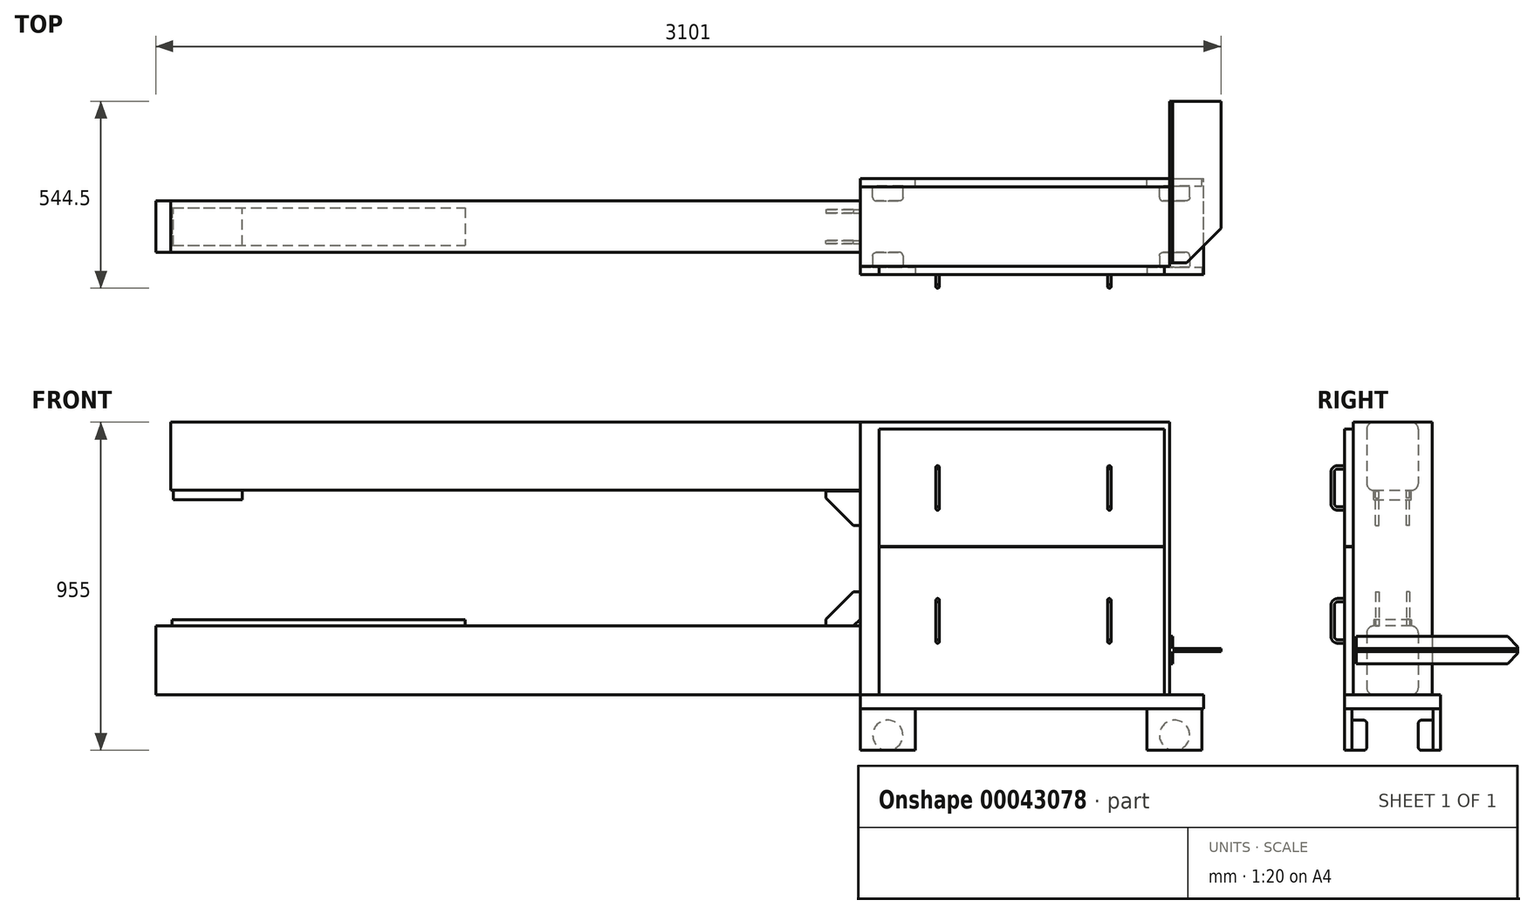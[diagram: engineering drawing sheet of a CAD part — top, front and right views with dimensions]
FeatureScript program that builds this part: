
annotation { "Feature Type Name" : "Feature", "Feature Type Description" : "" }
export const myFeature = defineFeature(function(context is Context, id is Id, definition is map)
    precondition{}
    {
        {
            var Q0;
            Q0=qCreatedBy(makeId("Front.planeOp"),FACE);
            var sketch = newSketch(context, id + "F0", { "sketchPlane" : qUnion([Q0])});
            skLineSegment(sketch, "E0.rect.bottom", {"start": v(-1025.5, 100) * mm, "end": v(1025.5, 100) * mm});
            skLineSegment(sketch, "E0.rect.top", {"start": v(-1025.5, -100) * mm, "end": v(1925.5, -100) * mm});
            skLineSegment(sketch, "E0.rect.left", {"start": v(-1025.5, 100) * mm, "end": v(-1025.5, -100) * mm});
            skLineSegment(sketch, "E0.rect.right", {"start": v(1025.5, 100) * mm, "end": v(1025.5, -100) * mm});
            skPoint(sketch, "E0.rect.middle", {"position": v(0, 0) * mm});
            skLineSegment(sketch, "E1.0", {"start": v(-982.5, 495) * mm, "end": v(1025.5, 495) * mm});
            skLineSegment(sketch, "E2.0", {"start": v(-982.5, 693) * mm, "end": v(1925.5, 693) * mm});
            skLineSegment(sketch, "E3.0", {"start": v(-982.5, 693) * mm, "end": v(-982.5, 495) * mm});
            skLineSegment(sketch, "E4", {"start": v(1025.5, 693) * mm, "end": v(1025.5, -100) * mm});
            skLineSegment(sketch, "E5.0", {"start": v(1925.5, 693) * mm, "end": v(1925.5, -100) * mm});
            skSolve(sketch);
        }
        {
            var Q0;
            {var subQ3=sQuery(id+"F0.wireOp",EDGE,"E1.0");Q0=makeQuery(id+"F0.imprint","IMPRINT",FACE,{"disambiguationData":[TD([[makeQuery(id+"F0.imprint","IMPRINT",EDGE,{"derivedFrom":subQ3}),1.0]])]});}
            var Q1;
            {var subQ3=sQuery(id+"F0.wireOp",EDGE,"E0.rect.bottom");Q1=makeQuery(id+"F0.imprint","IMPRINT",FACE,{"disambiguationData":[TD([[makeQuery(id+"F0.imprint","IMPRINT",EDGE,{"derivedFrom":subQ3}),-1.0]])]});}
            extrude(context, id + "F1", {"entities" : qUnion([Q0, Q1]), "endBound" : BoundingType.SYMMETRIC, "depth" : 150 * mm});
        }
        {
            var Q0;
            {var subQ0=sQuery(id+"F0.wireOp",EDGE,"E5.0");Q0=makeQuery(id+"F0.imprint","IMPRINT",FACE,{"disambiguationData":[TD([[makeQuery(id+"F0.imprint","IMPRINT",EDGE,{"derivedFrom":subQ0}),-1.0]])]});}
            extrude(context, id + "F2", {"entities" : qUnion([Q0]), "endBound" : BoundingType.SYMMETRIC, "depth" : 230 * mm});
        }
        {
            var Q0;
            Q0=makeQuery(id+"F1.opExtrude","CAP_EDGE",EDGE,{"disambiguationData":[OSD([sQuery(id+"F0.wireOp",EDGE,"E0.rect.bottom")])],"isStart":false});
            var Q1;
            Q1=makeQuery(id+"F1.opExtrude","CAP_EDGE",EDGE,{"disambiguationData":[OSD([sQuery(id+"F0.wireOp",EDGE,"E0.rect.top")])],"isStart":false});
            var Q2;
            Q2=makeQuery(id+"F1.opExtrude","CAP_EDGE",EDGE,{"disambiguationData":[OSD([sQuery(id+"F0.wireOp",EDGE,"E1.0")])],"isStart":false});
            var Q3;
            Q3=makeQuery(id+"F1.opExtrude","CAP_EDGE",EDGE,{"disambiguationData":[OSD([sQuery(id+"F0.wireOp",EDGE,"E2.0")])],"isStart":false});
            var Q4;
            Q4=makeQuery(id+"F1.opExtrude","CAP_EDGE",EDGE,{"disambiguationData":[OSD([sQuery(id+"F0.wireOp",EDGE,"E2.0")])],"isStart":true});
            var Q5;
            Q5=makeQuery(id+"F1.opExtrude","CAP_EDGE",EDGE,{"disambiguationData":[OSD([sQuery(id+"F0.wireOp",EDGE,"E1.0")])],"isStart":true});
            var Q6;
            Q6=makeQuery(id+"F1.opExtrude","CAP_EDGE",EDGE,{"disambiguationData":[OSD([sQuery(id+"F0.wireOp",EDGE,"E0.rect.bottom")])],"isStart":true});
            var Q7;
            Q7=makeQuery(id+"F1.opExtrude","CAP_EDGE",EDGE,{"disambiguationData":[OSD([sQuery(id+"F0.wireOp",EDGE,"E0.rect.top")])],"isStart":true});
            fillet(context, id + "F3", {"entities" : qUnion([Q0, Q1, Q2, Q3, Q4, Q5, Q6, Q7]), "radius" : 20 * mm, "tangentPropagation" : true, "allowEdgeOverflow" : false});
        }
        {
            var Q0;
            Q0=makeQuery(id+"F1.opExtrude","SWEPT_FACE",FACE,{"disambiguationData":[OSD([sQuery(id+"F0.wireOp",EDGE,"E0.rect.bottom")])]});
            var sketch = newSketch(context, id + "F4", { "sketchPlane" : qUnion([Q0])});
            skLineSegment(sketch, "E6.0", {"start": v(-978.5, -55) * mm, "end": v(-978.5, 55) * mm, "construction": true});
            skLineSegment(sketch, "E7.0", {"start": v(-124.5, -55) * mm, "end": v(-124.5, 55) * mm, "construction": true});
            skLineSegment(sketch, "E8.bottom", {"start": v(-978.5, 55) * mm, "end": v(-124.5, 55) * mm});
            skLineSegment(sketch, "E8.top", {"start": v(-978.5, -55) * mm, "end": v(-124.5, -55) * mm});
            skLineSegment(sketch, "E8.left", {"start": v(-978.5, 55) * mm, "end": v(-978.5, -55) * mm});
            skLineSegment(sketch, "E8.right", {"start": v(-124.5, 55) * mm, "end": v(-124.5, -55) * mm});
            skSolve(sketch);
        }
        {
            var Q0;
            Q0 = qSketchRegion(id + "F4", true);
            extrude(context, id + "F5", {"entities" : qUnion([Q0]), "operationType" : NewBodyOperationType.ADD, "depth" : 18 * mm});
        }
        {
            var Q0;
            Q0=makeQuery(id+"F1.opExtrude","SWEPT_FACE",FACE,{"disambiguationData":[OSD([sQuery(id+"F0.wireOp",EDGE,"E1.0")])]});
            var sketch = newSketch(context, id + "F6", { "sketchPlane" : qUnion([Q0])});
            skLineSegment(sketch, "E9.0", {"start": v(-974.5, 55) * mm, "end": v(-974.5, -55) * mm, "construction": true});
            skLineSegment(sketch, "E10.0", {"start": v(-774.5, 55) * mm, "end": v(-774.5, -55) * mm, "construction": true});
            skLineSegment(sketch, "E11.bottom", {"start": v(-974.5, 55) * mm, "end": v(-774.5, 55) * mm});
            skLineSegment(sketch, "E11.top", {"start": v(-974.5, -55) * mm, "end": v(-774.5, -55) * mm});
            skLineSegment(sketch, "E11.left", {"start": v(-974.5, 55) * mm, "end": v(-974.5, -55) * mm});
            skLineSegment(sketch, "E11.right", {"start": v(-774.5, 55) * mm, "end": v(-774.5, -55) * mm});
            skSolve(sketch);
        }
        {
            var Q0;
            Q0 = qSketchRegion(id + "F6", true);
            extrude(context, id + "F7", {"entities" : qUnion([Q0]), "operationType" : NewBodyOperationType.ADD, "depth" : 27 * mm});
        }
        {
            var Q0;
            Q0=qCreatedBy(makeId("Front.planeOp"),FACE);
            cPlane(context, id + "F8", {"entities" : qUnion([Q0]), "cplaneType" : CPlaneType.OFFSET, "offset" : 40 * mm, "width" : 150 * mm, "height" : 150 * mm});
        }
        {
            var Q0;
            Q0=qCreatedBy(id+"F8.planeOp",FACE);
            var sketch = newSketch(context, id + "F9", { "sketchPlane" : qUnion([Q0])});
            skLineSegment(sketch, "E12.0", {"start": v(-982.5, 495) * mm, "end": v(1025.5, 495) * mm, "construction": true});
            skLineSegment(sketch, "E13.0", {"start": v(1025.5, 693) * mm, "end": v(1025.5, -100) * mm, "construction": true});
            skLineSegment(sketch, "E14.0", {"start": v(-1025.5, 100) * mm, "end": v(1025.5, 100) * mm, "construction": true});
            skLineSegment(sketch, "E15.0", {"start": v(925.5, 693) * mm, "end": v(925.5, -100) * mm, "construction": true});
            skLineSegment(sketch, "E16.0", {"start": v(-1025.5, 200) * mm, "end": v(1025.5, 200) * mm, "construction": true});
            skLineSegment(sketch, "E17", {"start": v(1025.5, 296.5) * mm, "end": v(528.06, 296.5) * mm, "construction": true});
            skLineSegment(sketch, "E18.bottom", {"start": v(1005.5, 200) * mm, "end": v(1025.5, 200) * mm});
            skLineSegment(sketch, "E18.top", {"start": v(925.5, 100) * mm, "end": v(1025.5, 100) * mm});
            skLineSegment(sketch, "E18.left", {"start": v(925.5, 120) * mm, "end": v(925.5, 100) * mm});
            skLineSegment(sketch, "E18.right", {"start": v(1025.5, 200) * mm, "end": v(1025.5, 100) * mm, "construction": true});
            skLineSegment(sketch, "E19.0", {"start": v(1005.5, 200) * mm, "end": v(1005.5, 100) * mm, "construction": true});
            skLineSegment(sketch, "E20.0", {"start": v(925.5, 120) * mm, "end": v(1025.5, 120) * mm, "construction": true});
            skLineSegment(sketch, "E21", {"start": v(1005.5, 100) * mm, "end": v(1025.5, 120) * mm});
            skLineSegment(sketch, "E22", {"start": v(1005.5, 200) * mm, "end": v(925.5, 120) * mm});
            skLineSegment(sketch, "E23", {"start": v(1025.5, 200) * mm, "end": v(1025.5, 120) * mm});
            skLineSegment(sketch, "E24.MirrorCS", {"start": v(1005.5, 393) * mm, "end": v(1025.5, 393) * mm});
            skLineSegment(sketch, "E25.MirrorCS", {"start": v(1005.5, 493) * mm, "end": v(1025.5, 473) * mm});
            skLineSegment(sketch, "E26.MirrorCS", {"start": v(925.5, 473) * mm, "end": v(925.5, 493) * mm});
            skLineSegment(sketch, "E27.MirrorCS", {"start": v(1025.5, 393) * mm, "end": v(1025.5, 493) * mm});
            skLineSegment(sketch, "E28.MirrorCS", {"start": v(1025.5, 393) * mm, "end": v(1025.5, 473) * mm});
            skLineSegment(sketch, "E29.MirrorCS", {"start": v(1005.5, 393) * mm, "end": v(925.5, 473) * mm});
            skLineSegment(sketch, "E30.MirrorCS", {"start": v(925.5, 473) * mm, "end": v(1025.5, 473) * mm});
            skLineSegment(sketch, "E31.MirrorCS", {"start": v(925.5, 493) * mm, "end": v(1025.5, 493) * mm});
            skLineSegment(sketch, "E32.MirrorCS", {"start": v(1005.5, 393) * mm, "end": v(1005.5, 493) * mm});
            skSolve(sketch);
        }
        {
            var Q0;
            Q0 = qSketchRegion(id + "F9", true);
            extrude(context, id + "F10", {"entities" : qUnion([Q0]), "depth" : 10 * mm});
        }
        {
            var Q0;
            Q0=makeQuery(id+"F10.opExtrude","SWEPT_BODY",BODY,{"disambiguationData":[OSD([sQuery(id+"F9.wireOp",EDGE,"E24.MirrorCS"),sQuery(id+"F9.wireOp",EDGE,"E26.MirrorCS"),sQuery(id+"F9.wireOp",EDGE,"E27.MirrorCS"),sQuery(id+"F9.wireOp",EDGE,"E28.MirrorCS"),sQuery(id+"F9.wireOp",EDGE,"E29.MirrorCS"),sQuery(id+"F9.wireOp",EDGE,"E31.MirrorCS")])]});
            var Q1;
            Q1=makeQuery(id+"F10.opExtrude","SWEPT_BODY",BODY,{"disambiguationData":[OSD([sQuery(id+"F9.wireOp",EDGE,"E18.bottom"),sQuery(id+"F9.wireOp",EDGE,"E18.top"),sQuery(id+"F9.wireOp",EDGE,"E18.left"),sQuery(id+"F9.wireOp",EDGE,"E21"),sQuery(id+"F9.wireOp",EDGE,"E22"),sQuery(id+"F9.wireOp",EDGE,"E23")])]});
            var Q2;
            Q2=qCreatedBy(makeId("Front.planeOp"),FACE);
            mirror(context, id + "F11", {"entities" : qUnion([Q0, Q1]), "mirrorPlane" : qUnion([Q2])});
        }
        {
            var Q0;
            Q0=makeQuery(id+"F2.opExtrude","CAP_FACE",FACE,{"disambiguationData":[OSD([sQuery(id+"F0.wireOp",EDGE,"E0.rect.top"),sQuery(id+"F0.wireOp",EDGE,"E2.0"),sQuery(id+"F0.wireOp",EDGE,"E4"),sQuery(id+"F0.wireOp",EDGE,"E5.0")])],"isStart":false});
            var sketch = newSketch(context, id + "F12", { "sketchPlane" : qUnion([Q0])});
            skLineSegment(sketch, "E33.0", {"start": v(-982.5, 673) * mm, "end": v(1925.5, 673) * mm});
            skLineSegment(sketch, "E34.0", {"start": v(-982.5, 331) * mm, "end": v(1925.5, 331) * mm});
            skLineSegment(sketch, "E35.0", {"start": v(-982.5, 330) * mm, "end": v(1925.5, 330) * mm});
            skLineSegment(sketch, "E36.0", {"start": v(1020.5, 698) * mm, "end": v(1020.5, -105) * mm});
            skLineSegment(sketch, "E36.1", {"start": v(1930.5, 698) * mm, "end": v(1020.5, 698) * mm});
            skLineSegment(sketch, "E36.2", {"start": v(1930.5, -105) * mm, "end": v(1930.5, 698) * mm});
            skLineSegment(sketch, "E36.3", {"start": v(1020.5, -105) * mm, "end": v(1930.5, -105) * mm});
            skLineSegment(sketch, "E37.0", {"start": v(-982.5, -108) * mm, "end": v(1925.5, -108) * mm});
            skLineSegment(sketch, "E38.0", {"start": v(1079.5, 693) * mm, "end": v(1079.5, -100) * mm});
            skLineSegment(sketch, "E39.0", {"start": v(1910.5, -105) * mm, "end": v(1910.5, 698) * mm});
            skSolve(sketch);
        }
        {
            var Q0;
            {var subQ3=sQuery(id+"F12.wireOp",EDGE,"E33.0");var subQ5=sQuery(id+"F12.wireOp",EDGE,"E38.0");var subQ7=makeQuery(id+"F12.imprint","INTERSECT",VERTEX,{"derivedFrom":[subQ3,subQ5]});Q0=makeQuery(id+"F12.imprint","IMPRINT",FACE,{"disambiguationData":[TD([[makeQuery(id+"F12.imprint","IMPRINT",EDGE,{"disambiguationData":[TD([[subQ7,-1.0]])],"derivedFrom":subQ3}),-1.0]])]});}
            var Q1;
            {var subQ3=sQuery(id+"F12.wireOp",EDGE,"E38.0");var subQ5=sQuery(id+"F12.wireOp",EDGE,"E35.0");var subQ7=makeQuery(id+"F12.imprint","INTERSECT",VERTEX,{"derivedFrom":[subQ5,subQ3]});Q1=makeQuery(id+"F12.imprint","IMPRINT",FACE,{"disambiguationData":[TD([[makeQuery(id+"F12.imprint","IMPRINT",EDGE,{"disambiguationData":[TD([[subQ7,-1.0]])],"derivedFrom":subQ5}),-1.0]])]});}
            extrude(context, id + "F13", {"entities" : qUnion([Q0, Q1]), "operationType" : NewBodyOperationType.ADD, "depth" : 25 * mm});
        }
        {
            var Q0;
            Q0=makeQuery(id+"F2.opExtrude","SWEPT_FACE",FACE,{"disambiguationData":[OSD([sQuery(id+"F0.wireOp",EDGE,"E5.0")])]});
            cPlane(context, id + "F14", {"entities" : qUnion([Q0]), "cplaneType" : CPlaneType.OFFSET, "offset" : 175 * mm, "oppositeDirection" : true, "width" : 150 * mm, "height" : 150 * mm});
        }
        {
            var Q0;
            Q0=qCreatedBy(id+"F14.planeOp",FACE);
            cPlane(context, id + "F15", {"entities" : qUnion([Q0]), "cplaneType" : CPlaneType.OFFSET, "offset" : 250 * mm, "oppositeDirection" : true, "width" : 150 * mm, "height" : 150 * mm});
        }
        {
            var Q0;
            Q0=qCreatedBy(id+"F14.planeOp",FACE);
            var sketch = newSketch(context, id + "F16", { "sketchPlane" : qUnion([Q0])});
            skLineSegment(sketch, "E40.0", {"start": v(-140, 331) * mm, "end": v(-140, 673) * mm, "construction": true});
            skLineSegment(sketch, "E41.0", {"start": v(-140, -100) * mm, "end": v(-140, 330) * mm, "construction": true});
            skLineSegment(sketch, "E42", {"start": v(-140, 502) * mm, "end": v(-356.24, 502) * mm, "construction": true});
            skLineSegment(sketch, "E43", {"start": v(-140, 115) * mm, "end": v(-344.44, 115) * mm, "construction": true});
            skLineSegment(sketch, "E44.0", {"start": v(-140, 562) * mm, "end": v(-159.5, 562) * mm});
            skLineSegment(sketch, "E45.0", {"start": v(-140, 175) * mm, "end": v(-344.44, 175) * mm, "construction": true});
            skLineSegment(sketch, "E46.0", {"start": v(-174.5, 502) * mm, "end": v(-174.5, 562) * mm, "construction": true});
            skLineSegment(sketch, "E47", {"start": v(-174.5, 160) * mm, "end": v(-174.5, 115) * mm});
            skLineSegment(sketch, "E48", {"start": v(-159.5, 175) * mm, "end": v(-140, 175) * mm});
            skLineSegment(sketch, "E49", {"start": v(-174.5, 502) * mm, "end": v(-174.5, 547) * mm});
            skPoint(sketch, "E50.visualSharp", {"position": v(-174.5, 175) * mm});
            skArc(sketch, "E50.filletArc", {"start": v(-159.5, 175) * mm, "mid": v(-170.1, 170.6) * mm, "end": v(-174.5, 160) * mm});
            skArc(sketch, "E51.filletArc", {"start": v(-159.5, 562) * mm, "mid": v(-170.1, 557.6) * mm, "end": v(-174.5, 547) * mm});
            skLineSegment(sketch, "E52.MirrorCS", {"start": v(-174.5, 502) * mm, "end": v(-174.5, 457) * mm});
            skLineSegment(sketch, "E53.MirrorCS", {"start": v(-140, 442) * mm, "end": v(-159.5, 442) * mm});
            skArc(sketch, "E54.MirrorCS", {"start": v(-159.5, 442) * mm, "mid": v(-170.1, 446.4) * mm, "end": v(-174.5, 457) * mm});
            skPoint(sketch, "E55.orphan", {"position": v(-174.5, 442) * mm});
            skArc(sketch, "E56.MirrorCS", {"start": v(-159.5, 55) * mm, "mid": v(-170.1, 59.4) * mm, "end": v(-174.5, 70) * mm});
            skPoint(sketch, "E57.MirrorP", {"position": v(-174.5, 55) * mm});
            skLineSegment(sketch, "E58.MirrorCS", {"start": v(-159.5, 55) * mm, "end": v(-140, 55) * mm});
            skLineSegment(sketch, "E59.MirrorCS", {"start": v(-174.5, 70) * mm, "end": v(-174.5, 115) * mm});
            skSolve(sketch);
        }
        {
            var Q0;
            Q0=makeQuery(id+"F13.opExtrude","CAP_FACE",FACE,{"disambiguationData":[OSD([sQuery(id+"F12.wireOp",EDGE,"E33.0"),sQuery(id+"F12.wireOp",EDGE,"E34.0"),sQuery(id+"F12.wireOp",EDGE,"E38.0"),sQuery(id+"F12.wireOp",EDGE,"E39.0")])],"isStart":false});
            var sketch = newSketch(context, id + "F17", { "sketchPlane" : qUnion([Q0])});
            skPoint(sketch, "E60.0", {"position": v(1750.5, 562) * mm});
            skPoint(sketch, "E61.0", {"position": v(1750.5, 175) * mm});
            skCircle(sketch, "E62", {"center": v(1750.5, 562) * mm, "radius": 5 * mm});
            skCircle(sketch, "E63", {"center": v(1750.5, 175) * mm, "radius": 5 * mm});
            skSolve(sketch);
        }
        {
            var Q0;
            Q0=makeQuery(id+"F17.imprint","IMPRINT",FACE,{"disambiguationData":[TD([[makeQuery(id+"F17.imprint","IMPRINT",EDGE,{"derivedFrom":sQuery(id+"F17.wireOp",EDGE,"E62")}),1.0]])]});
            var Q1;
            Q1=sQuery(id+"F16.wireOp",EDGE,"E44.0");
            var Q2;
            Q2=sQuery(id+"F16.wireOp",EDGE,"E51.filletArc");
            var Q3;
            Q3=sQuery(id+"F16.wireOp",EDGE,"E49");
            var Q4;
            Q4=sQuery(id+"F16.wireOp",EDGE,"E52.MirrorCS");
            var Q5;
            Q5=sQuery(id+"F16.wireOp",EDGE,"E54.MirrorCS");
            var Q6;
            Q6=sQuery(id+"F16.wireOp",EDGE,"E53.MirrorCS");
            sweep(context, id + "F18", {"profiles" : qUnion([Q0]), "path" : qUnion([Q1, Q2, Q3, Q4, Q5, Q6])});
        }
        {
            var Q0;
            Q0=makeQuery(id+"F17.imprint","IMPRINT",FACE,{"disambiguationData":[TD([[makeQuery(id+"F17.imprint","IMPRINT",EDGE,{"derivedFrom":sQuery(id+"F17.wireOp",EDGE,"E63")}),1.0]])]});
            var Q1;
            Q1=sQuery(id+"F16.wireOp",EDGE,"E48");
            var Q2;
            Q2=sQuery(id+"F16.wireOp",EDGE,"E50.filletArc");
            var Q3;
            Q3=sQuery(id+"F16.wireOp",EDGE,"E47");
            var Q4;
            Q4=sQuery(id+"F16.wireOp",EDGE,"E59.MirrorCS");
            var Q5;
            Q5=sQuery(id+"F16.wireOp",EDGE,"E56.MirrorCS");
            var Q6;
            Q6=sQuery(id+"F16.wireOp",EDGE,"E58.MirrorCS");
            sweep(context, id + "F19", {"profiles" : qUnion([Q0]), "path" : qUnion([Q1, Q2, Q3, Q4, Q5, Q6])});
        }
        {
            var Q0;
            Q0=makeQuery(id+"F19.opSweep","SWEPT_BODY",BODY,{"disambiguationData":[OSD([sQuery(id+"F16.wireOp",EDGE,"E58.MirrorCS"),sQuery(id+"F17.wireOp",EDGE,"E63")])]});
            var Q1;
            Q1=makeQuery(id+"F18.opSweep","SWEPT_BODY",BODY,{"disambiguationData":[OSD([sQuery(id+"F16.wireOp",EDGE,"E53.MirrorCS"),sQuery(id+"F17.wireOp",EDGE,"E62")])]});
            var Q2;
            Q2=qCreatedBy(id+"F15.planeOp",FACE);
            mirror(context, id + "F20", {"operationType" : NewBodyOperationType.ADD, "entities" : qUnion([Q0, Q1]), "mirrorPlane" : qUnion([Q2])});
        }
        {
            var Q0;
            Q0=makeQuery(id+"F2.opExtrude","SWEPT_FACE",FACE,{"disambiguationData":[OSD([sQuery(id+"F0.wireOp",EDGE,"E5.0")])]});
            cPlane(context, id + "F21", {"entities" : qUnion([Q0]), "cplaneType" : CPlaneType.OFFSET, "offset" : 100 * mm, "width" : 150 * mm, "height" : 150 * mm});
        }
        {
            var Q0;
            Q0=qCreatedBy(id+"F21.planeOp",FACE);
            var sketch = newSketch(context, id + "F22", { "sketchPlane" : qUnion([Q0])});
            skLineSegment(sketch, "E64", {"start": v(0, 0) * mm, "end": v(0, -281) * mm, "construction": true});
            skLineSegment(sketch, "E65.0", {"start": v(-140, 0) * mm, "end": v(-140, -277.75) * mm, "construction": true});
            skLineSegment(sketch, "E66.0.0", {"start": v(115, -100) * mm, "end": v(115, 693) * mm, "construction": true});
            skLineSegment(sketch, "E66.0.1", {"start": v(115, 693) * mm, "end": v(-115, 693) * mm, "construction": true});
            skLineSegment(sketch, "E66.0.2", {"start": v(-115, 693) * mm, "end": v(-115, -100) * mm, "construction": true});
            skLineSegment(sketch, "E66.0.3", {"start": v(-115, -100) * mm, "end": v(115, -100) * mm, "construction": true});
            skPoint(sketch, "E67.oppositeSnap0", {"position": v(0, -140.5) * mm});
            skLineSegment(sketch, "E67.bottom", {"start": v(-140, -100) * mm, "end": v(140, -100) * mm});
            skLineSegment(sketch, "E67.top", {"start": v(-140, -140.5) * mm, "end": v(140, -140.5) * mm});
            skLineSegment(sketch, "E67.left", {"start": v(-140, -100) * mm, "end": v(-140, -140.5) * mm});
            skLineSegment(sketch, "E67.right", {"start": v(140, -100) * mm, "end": v(140, -140.5) * mm});
            skSolve(sketch);
        }
        {
            var Q0;
            Q0 = qSketchRegion(id + "F22", true);
            extrude(context, id + "F23", {"entities" : qUnion([Q0]), "oppositeDirection" : true, "depth" : 1000 * mm});
        }
        {
            var Q0;
            Q0=makeQuery(id+"F23.opExtrude","SWEPT_FACE",FACE,{"disambiguationData":[OSD([sQuery(id+"F22.wireOp",EDGE,"E67.left")])]});
            var sketch = newSketch(context, id + "F24", { "sketchPlane" : qUnion([Q0])});
            skLineSegment(sketch, "E68.bottom", {"start": v(2020.5, -140.5) * mm, "end": v(1860.5, -140.5) * mm});
            skLineSegment(sketch, "E68.top", {"start": v(2020.5, -262) * mm, "end": v(1860.5, -262) * mm});
            skLineSegment(sketch, "E68.left", {"start": v(2020.5, -140.5) * mm, "end": v(2020.5, -262) * mm});
            skLineSegment(sketch, "E68.right", {"start": v(1860.5, -140.5) * mm, "end": v(1860.5, -262) * mm});
            skLineSegment(sketch, "E69.0.0", {"start": v(2025.5, -140.5) * mm, "end": v(2025.5, -100) * mm, "construction": true});
            skLineSegment(sketch, "E69.0.1", {"start": v(2025.5, -100) * mm, "end": v(1025.5, -100) * mm, "construction": true});
            skLineSegment(sketch, "E69.0.2", {"start": v(1025.5, -100) * mm, "end": v(1025.5, -140.5) * mm, "construction": true});
            skLineSegment(sketch, "E69.0.3", {"start": v(1025.5, -140.5) * mm, "end": v(2025.5, -140.5) * mm, "construction": true});
            skLineSegment(sketch, "E70.bottom", {"start": v(1025.5, -140.5) * mm, "end": v(1185.5, -140.5) * mm});
            skLineSegment(sketch, "E70.top", {"start": v(1025.5, -262) * mm, "end": v(1185.5, -262) * mm});
            skLineSegment(sketch, "E70.left", {"start": v(1025.5, -140.5) * mm, "end": v(1025.5, -262) * mm});
            skLineSegment(sketch, "E70.right", {"start": v(1185.5, -140.5) * mm, "end": v(1185.5, -262) * mm});
            skSolve(sketch);
        }
        {
            var Q0;
            Q0 = qSketchRegion(id + "F24", true);
            extrude(context, id + "F25", {"entities" : qUnion([Q0]), "oppositeDirection" : true, "depth" : 22 * mm});
        }
        {
            var Q0;
            Q0=makeQuery(id+"F25.opExtrude","CAP_FACE",FACE,{"disambiguationData":[OSD([sQuery(id+"F24.wireOp",EDGE,"E70.bottom"),sQuery(id+"F24.wireOp",EDGE,"E70.top"),sQuery(id+"F24.wireOp",EDGE,"E70.left"),sQuery(id+"F24.wireOp",EDGE,"E70.right")])],"isStart":false});
            var sketch = newSketch(context, id + "F26", { "sketchPlane" : qUnion([Q0])});
            skLineSegment(sketch, "E71.0.0", {"start": v(-1025.5, -262) * mm, "end": v(-1025.5, -140.5) * mm, "construction": true});
            skLineSegment(sketch, "E71.0.1", {"start": v(-1025.5, -140.5) * mm, "end": v(-1185.5, -140.5) * mm, "construction": true});
            skLineSegment(sketch, "E71.0.2", {"start": v(-1185.5, -140.5) * mm, "end": v(-1185.5, -262) * mm, "construction": true});
            skLineSegment(sketch, "E71.0.3", {"start": v(-1185.5, -262) * mm, "end": v(-1025.5, -262) * mm, "construction": true});
            skLineSegment(sketch, "E72.0", {"start": v(-1025.5, -218) * mm, "end": v(-1185.5, -218) * mm, "construction": true});
            skCircle(sketch, "E73", {"center": v(-1105.5, -218) * mm, "radius": 44 * mm});
            skLineSegment(sketch, "E74.1.0", {"start": v(-2020.5, -262) * mm, "end": v(-1860.5, -262) * mm, "construction": true});
            skLineSegment(sketch, "E74.1.1", {"start": v(-1860.5, -262) * mm, "end": v(-1860.5, -140.5) * mm, "construction": true});
            skLineSegment(sketch, "E74.1.2", {"start": v(-1860.5, -140.5) * mm, "end": v(-2020.5, -140.5) * mm, "construction": true});
            skLineSegment(sketch, "E74.1.3", {"start": v(-2020.5, -140.5) * mm, "end": v(-2020.5, -262) * mm, "construction": true});
            skLineSegment(sketch, "E75", {"start": v(-1860.5, -201.25) * mm, "end": v(-1185.5, -201.25) * mm, "construction": true});
            skLineSegment(sketch, "E76", {"start": v(-1523, -201.25) * mm, "end": v(-1523, -366.76) * mm, "construction": true});
            skCircle(sketch, "E77.MirrorC", {"center": v(-1940.5, -218) * mm, "radius": 44 * mm});
            skSolve(sketch);
        }
        {
            var Q0;
            Q0 = qSketchRegion(id + "F26", true);
            extrude(context, id + "F27", {"entities" : qUnion([Q0]), "depth" : 43 * mm});
        }
        {
            var Q0;
            Q0=makeQuery(id+"F27.opExtrude","CAP_FACE",FACE,{"disambiguationData":[OSD([sQuery(id+"F26.wireOp",EDGE,"E73")])],"isStart":false});
            var Q1;
            Q1=makeQuery(id+"F27.opExtrude","CAP_FACE",FACE,{"disambiguationData":[OSD([sQuery(id+"F26.wireOp",EDGE,"E77.MirrorC")])],"isStart":false});
            fillet(context, id + "F28", {"entities" : qUnion([Q0, Q1]), "radius" : 10 * mm, "tangentPropagation" : true, "allowEdgeOverflow" : false});
        }
        {
            var Q0;
            Q0=makeQuery(id+"F25.opExtrude","SWEPT_BODY",BODY,{"disambiguationData":[OSD([sQuery(id+"F24.wireOp",EDGE,"E68.bottom"),sQuery(id+"F24.wireOp",EDGE,"E68.top"),sQuery(id+"F24.wireOp",EDGE,"E68.left"),sQuery(id+"F24.wireOp",EDGE,"E68.right")])]});
            var Q1;
            Q1=makeQuery(id+"F25.opExtrude","SWEPT_BODY",BODY,{"disambiguationData":[OSD([sQuery(id+"F24.wireOp",EDGE,"E70.bottom"),sQuery(id+"F24.wireOp",EDGE,"E70.top"),sQuery(id+"F24.wireOp",EDGE,"E70.left"),sQuery(id+"F24.wireOp",EDGE,"E70.right")])]});
            var Q2;
            Q2=makeQuery(id+"F27.opExtrude","SWEPT_BODY",BODY,{"disambiguationData":[OSD([sQuery(id+"F26.wireOp",EDGE,"E77.MirrorC")])]});
            var Q3;
            Q3=makeQuery(id+"F27.opExtrude","SWEPT_BODY",BODY,{"disambiguationData":[OSD([sQuery(id+"F26.wireOp",EDGE,"E73")])]});
            var Q4;
            Q4=qCreatedBy(makeId("Front.planeOp"),FACE);
            mirror(context, id + "F29", {"entities" : qUnion([Q0, Q1, Q2, Q3]), "mirrorPlane" : qUnion([Q4])});
        }
        {
            var Q0;
            Q0=makeQuery(id+"F2.opExtrude","SWEPT_FACE",FACE,{"disambiguationData":[OSD([sQuery(id+"F0.wireOp",EDGE,"E5.0")])]});
            var sketch = newSketch(context, id + "F30", { "sketchPlane" : qUnion([Q0])});
            skLineSegment(sketch, "E78.0", {"start": v(-140, -100) * mm, "end": v(140, -100) * mm, "construction": true});
            skLineSegment(sketch, "E79.0", {"start": v(-105, -10) * mm, "end": v(365, -10) * mm});
            skLineSegment(sketch, "E80.0", {"start": v(-105, 70) * mm, "end": v(365, 70) * mm});
            skLineSegment(sketch, "E81.0", {"start": v(365, 70) * mm, "end": v(365, -10) * mm});
            skLineSegment(sketch, "E82.0", {"start": v(-105, 70) * mm, "end": v(-105, -10) * mm});
            skSolve(sketch);
        }
        {
            var Q0;
            Q0 = qSketchRegion(id + "F30", true);
            extrude(context, id + "F31", {"entities" : qUnion([Q0]), "operationType" : NewBodyOperationType.ADD, "depth" : 10 * mm});
        }
        {
            var Q0;
            Q0=makeQuery(id+"F31.opExtrude","SWEPT_EDGE",EDGE,{"disambiguationData":[OSD([sQuery(id+"F30.wireOp",EDGE,"E80.0"),sQuery(id+"F30.wireOp",EDGE,"E81.0")])]});
            var Q1;
            Q1=makeQuery(id+"F31.opExtrude","SWEPT_EDGE",EDGE,{"disambiguationData":[OSD([sQuery(id+"F30.wireOp",EDGE,"E79.0"),sQuery(id+"F30.wireOp",EDGE,"E81.0")])]});
            chamfer(context, id + "F32", {"entities" : qUnion([Q0, Q1]), "width" : 30 * mm, "tangentPropagation" : true});
        }
        {
            var Q0;
            Q0=makeQuery(id+"F31.opExtrude","CAP_FACE",FACE,{"disambiguationData":[OSD([sQuery(id+"F30.wireOp",EDGE,"E79.0"),sQuery(id+"F30.wireOp",EDGE,"E80.0"),sQuery(id+"F30.wireOp",EDGE,"E81.0"),sQuery(id+"F30.wireOp",EDGE,"E82.0")])],"isStart":false});
            var sketch = newSketch(context, id + "F33", { "sketchPlane" : qUnion([Q0])});
            skLineSegment(sketch, "E83", {"start": v(365, 30) * mm, "end": v(-105, 30) * mm, "construction": true});
            skLineSegment(sketch, "E84.0", {"start": v(365, 35) * mm, "end": v(-105, 35) * mm});
            skLineSegment(sketch, "E85.0", {"start": v(365, 25) * mm, "end": v(-105, 25) * mm});
            skLineSegment(sketch, "E86", {"start": v(-105, 35) * mm, "end": v(-105, 25) * mm});
            skLineSegment(sketch, "E87", {"start": v(365, 35) * mm, "end": v(365, 25) * mm});
            skSolve(sketch);
        }
        {
            var Q0;
            Q0 = qSketchRegion(id + "F33", true);
            extrude(context, id + "F34", {"entities" : qUnion([Q0]), "operationType" : NewBodyOperationType.ADD, "depth" : 140 * mm});
        }
        {
            var Q0;
            Q0=makeQuery(id+"F34.opExtrude","CAP_EDGE",EDGE,{"disambiguationData":[OSD([sQuery(id+"F33.wireOp",EDGE,"E86")])],"isStart":false});
            chamfer(context, id + "F35", {"entities" : qUnion([Q0]), "width" : 100 * mm, "tangentPropagation" : true});
        }
    });
